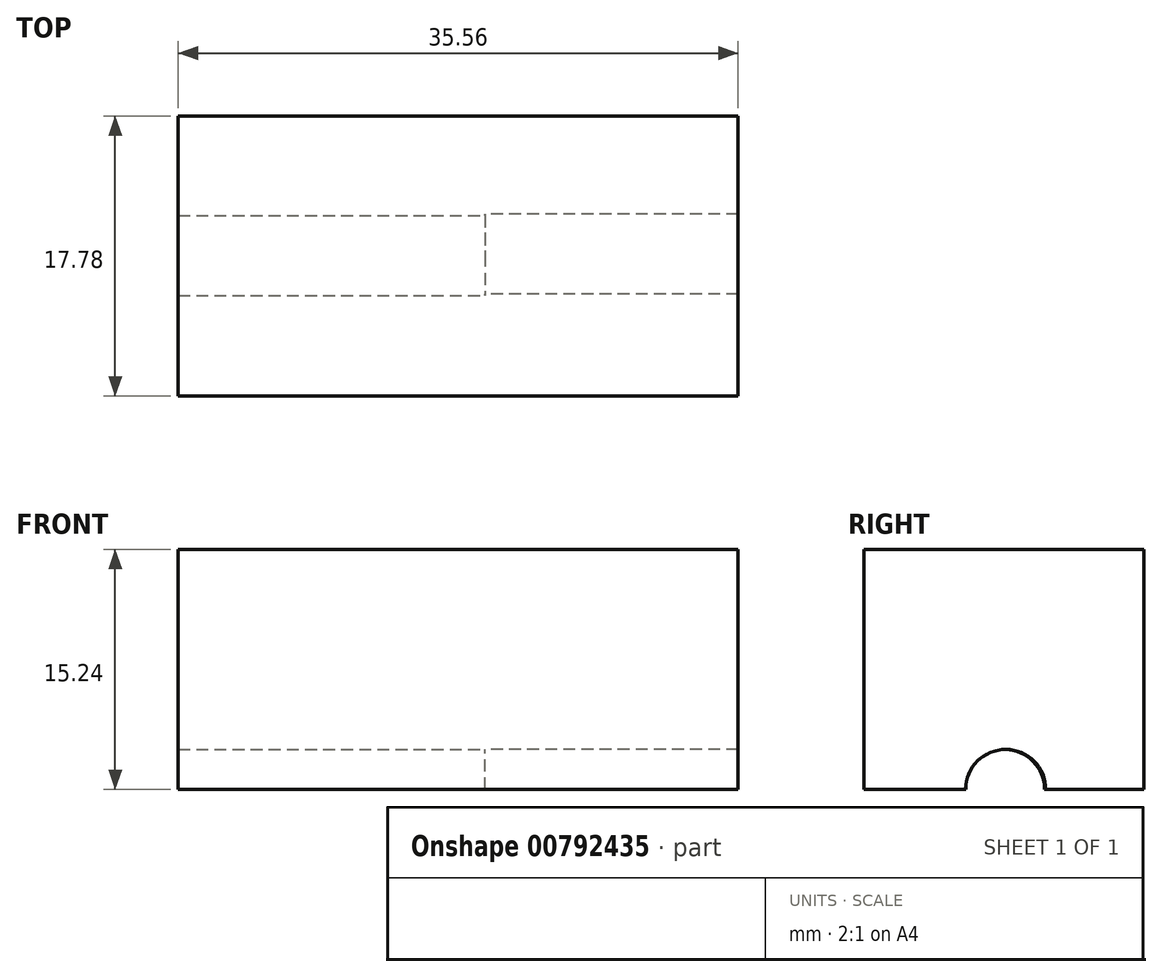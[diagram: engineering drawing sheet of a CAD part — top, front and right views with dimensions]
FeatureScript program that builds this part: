
annotation { "Feature Type Name" : "Feature", "Feature Type Description" : "" }
export const myFeature = defineFeature(function(context is Context, id is Id, definition is map)
    precondition{}
    {
        {
            var Q0;
            Q0=qCreatedBy(makeId("Front.planeOp"),FACE);
            var sketch = newSketch(context, id + "F0", { "sketchPlane" : qUnion([Q0])});
            skLineSegment(sketch, "E0", {"start": v(-19.48, 0) * mm, "end": v(16.08, 0) * mm});
            skLineSegment(sketch, "E1", {"start": v(16.08, 0) * mm, "end": v(16.08, 15.24) * mm});
            skLineSegment(sketch, "E2", {"start": v(16.08, 15.24) * mm, "end": v(-19.48, 15.24) * mm});
            skLineSegment(sketch, "E3", {"start": v(-19.48, 15.24) * mm, "end": v(-19.48, 0) * mm});
            skSolve(sketch);
        }
        {
            var Q0;
            Q0 = qSketchRegion(id + "F0", true);
            extrude(context, id + "F1", {"entities" : qUnion([Q0]), "depth" : 17.78 * mm, "offsetDistance" : 25.4 * mm});
        }
        {
            var Q0;
            Q0=qCreatedBy(makeId("Right.planeOp"),FACE);
            var sketch = newSketch(context, id + "F2", { "sketchPlane" : qUnion([Q0])});
            skCircle(sketch, "E4", {"center": v(-8.78, 0) * mm, "radius": 2.54 * mm});
            skSolve(sketch);
        }
        {
            var Q0;
            Q0 = qSketchRegion(id + "F2", true);
            extrude(context, id + "F3", {"entities" : qUnion([Q0]), "operationType" : NewBodyOperationType.REMOVE, "depth" : 25.4 * mm, "offsetDistance" : 25.4 * mm});
        }
        {
            var Q0;
            Q0=qCreatedBy(makeId("Right.planeOp"),FACE);
            var sketch = newSketch(context, id + "F4", { "sketchPlane" : qUnion([Q0])});
            skCircle(sketch, "E5", {"center": v(-8.86, 0) * mm, "radius": 2.54 * mm});
            skSolve(sketch);
        }
        {
            var Q0;
            Q0 = qSketchRegion(id + "F4", true);
            extrude(context, id + "F5", {"entities" : qUnion([Q0]), "operationType" : NewBodyOperationType.REMOVE, "oppositeDirection" : true, "depth" : 25.4 * mm, "offsetDistance" : 25.4 * mm});
        }
    });
